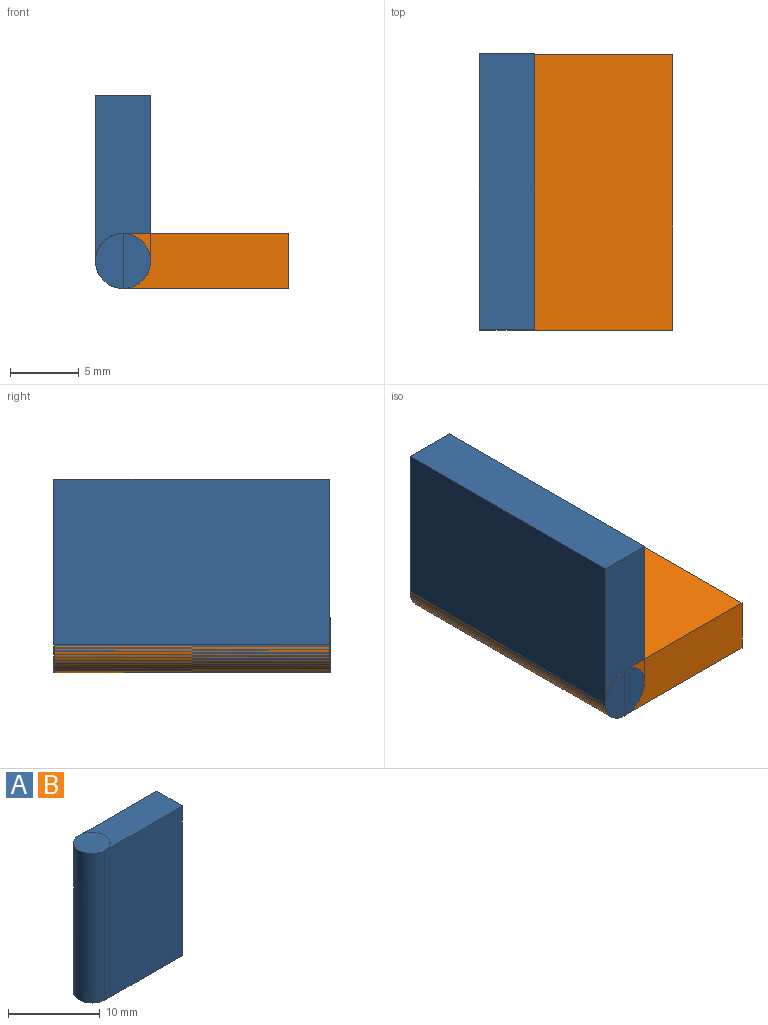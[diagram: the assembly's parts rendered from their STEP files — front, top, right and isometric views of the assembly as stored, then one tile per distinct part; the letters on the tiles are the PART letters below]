
ASSEMBLY  parts=2 mates=1
PART A: 9 faces, bbox 14x4x20 mm
  f0: cylinder r=2mm len=20mm, axis (0,0,-1), area 126mm2, adj f1,f2,f6,f7,f8
  f1: plane 4x2mm, normal (0,0,-1), area 6.3mm2, adj f0,f3
  f2: plane 4x4mm, normal (0,0,1), area 12.6mm2, adj f0
  f3: plane 4x0.05mm, normal (-1,0,0), area 0.2mm2, adj f1,f4,f7,f8
  f4: plane 12x4mm, normal (0,0,-1), area 48mm2, adj f3,f5,f7,f8
  f5: plane 20x4mm, normal (1,0,0), area 80mm2, adj f4,f6,f7,f8
  f6: plane 12x4mm, normal (0,0,1), area 41.7mm2, adj f0,f5,f7,f8
  f7: plane 20x12mm, normal (0,-1,0), area 240mm2, adj f0,f3,f4,f5,f6
  f8: plane 20x12mm, normal (0,1,0), area 240mm2, adj f0,f3,f4,f5,f6
PART B: same geometry as A
PLACE A rot(axis=(0.58,-0.58,0.58),120deg) t=(0,-0.02,-2)mm
PLACE B rot(axis=(-1,0,0),90deg) t=(0,0.02,-2)mm
MATE revolute A.f0 <-> B.f0  axis (0,-1,0) through (0,-10.02,-2)mm
